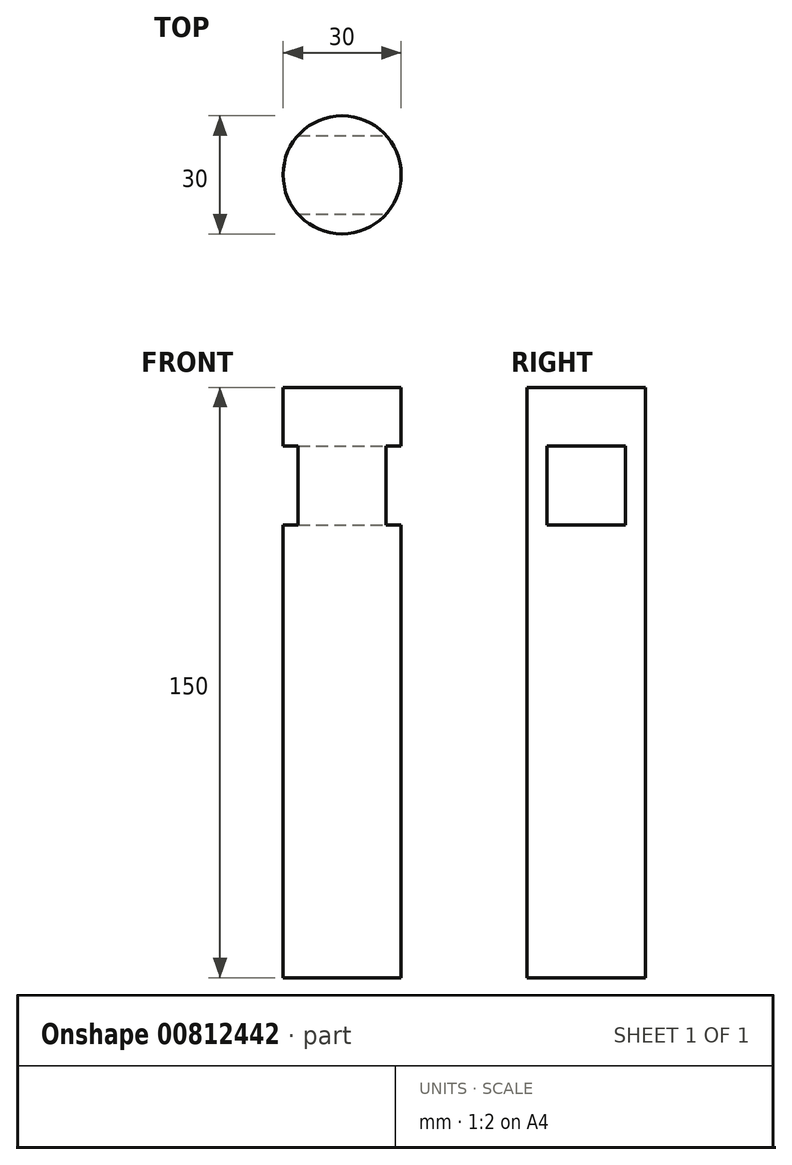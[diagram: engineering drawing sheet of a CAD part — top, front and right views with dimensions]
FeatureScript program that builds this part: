
annotation { "Feature Type Name" : "Feature", "Feature Type Description" : "" }
export const myFeature = defineFeature(function(context is Context, id is Id, definition is map)
    precondition{}
    {
        {
            var Q0;
            Q0=qCreatedBy(makeId("Top.planeOp"),FACE);
            var sketch = newSketch(context, id + "F0", { "sketchPlane" : qUnion([Q0])});
            skCircle(sketch, "E0", {"center": v(0, 0) * mm, "radius": 15 * mm});
            skLineSegment(sketch, "E1", {"start": v(0, 0) * mm, "end": v(70.48, -442.59) * mm});
            skSolve(sketch);
        }
        {
            var Q0;
            Q0=makeQuery(id+"F0.imprint","IMPRINT",FACE,{"disambiguationData":[TD([[makeQuery(id+"F0.imprint","IMPRINT",EDGE,{"derivedFrom":sQuery(id+"F0.wireOp",EDGE,"E0")}),1.0]])]});
            extrude(context, id + "F1", {"entities" : qUnion([Q0]), "depth" : 150 * mm, "offsetDistance" : 25 * mm});
        }
        {
            var Q0;
            Q0=qCreatedBy(makeId("Right.planeOp"),FACE);
            var sketch = newSketch(context, id + "F2", { "sketchPlane" : qUnion([Q0])});
            skLineSegment(sketch, "E2", {"start": v(0, 0) * mm, "end": v(0, 170.73) * mm});
            skLineSegment(sketch, "E3.bottom", {"start": v(10, 135.08) * mm, "end": v(-10, 135.08) * mm});
            skLineSegment(sketch, "E3.top", {"start": v(10, 115.08) * mm, "end": v(-10, 115.08) * mm});
            skLineSegment(sketch, "E3.left", {"start": v(10, 135.08) * mm, "end": v(10, 115.08) * mm});
            skLineSegment(sketch, "E3.right", {"start": v(-10, 135.08) * mm, "end": v(-10, 115.08) * mm});
            skSolve(sketch);
        }
        {
            var Q0;
            Q0 = qSketchRegion(id + "F2", true);
            extrude(context, id + "F3", {"entities" : qUnion([Q0]), "operationType" : NewBodyOperationType.REMOVE, "endBound" : BoundingType.UP_TO_NEXT, "oppositeDirection" : true, "depth" : 25 * mm, "offsetDistance" : 25 * mm, "hasSecondDirection" : true, "secondDirectionBound" : SecondDirectionBoundingType.UP_TO_NEXT, "secondDirectionOppositeDirection" : false, "secondDirectionDepth" : 25 * mm});
        }
    });
